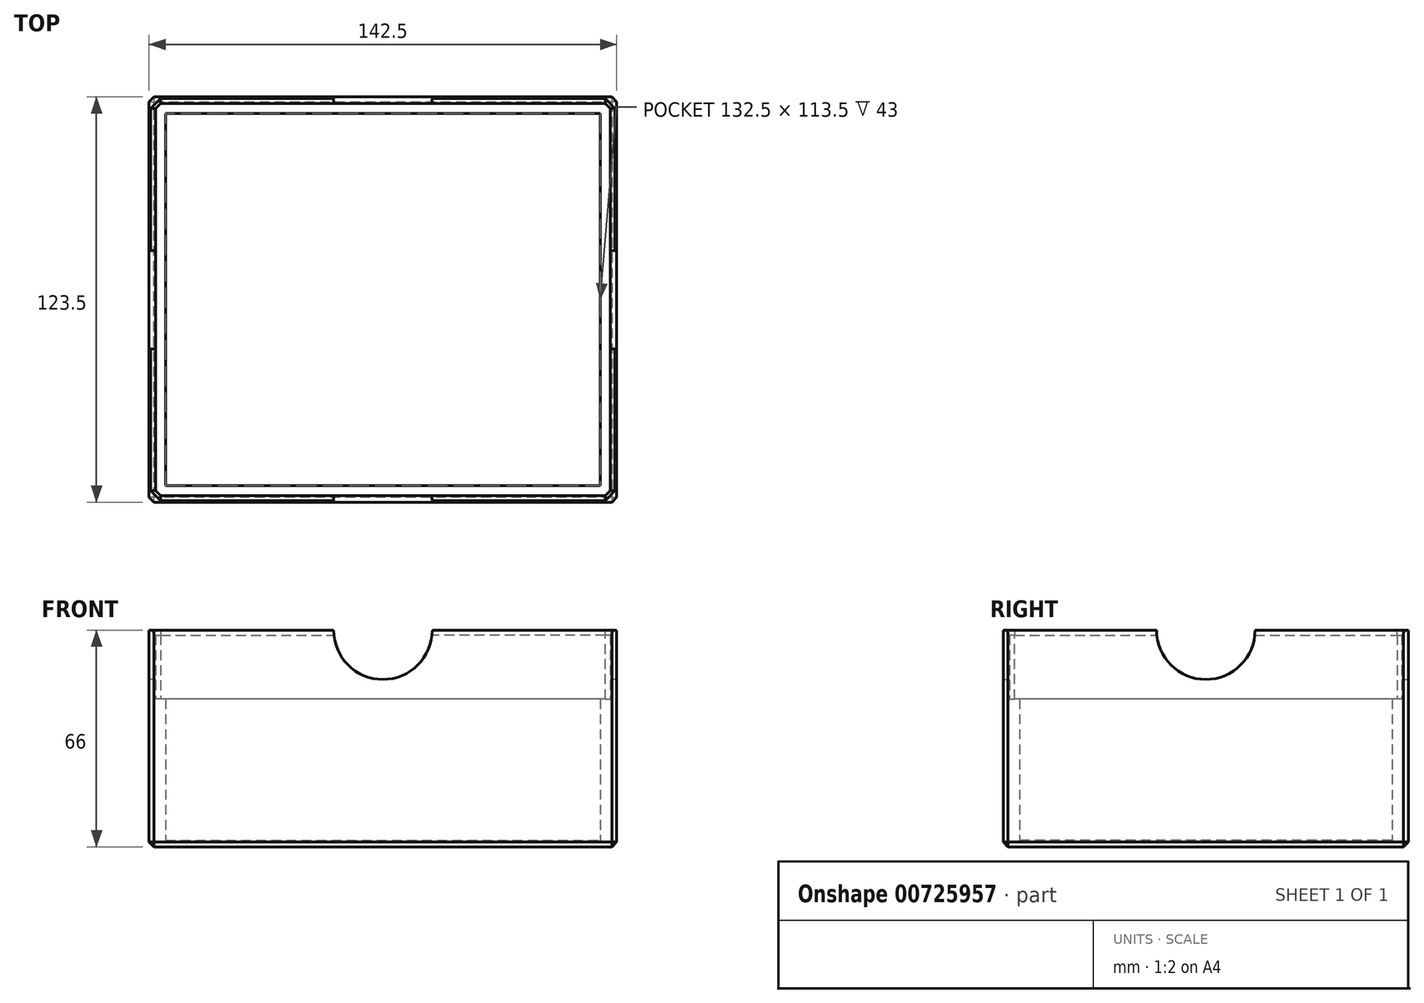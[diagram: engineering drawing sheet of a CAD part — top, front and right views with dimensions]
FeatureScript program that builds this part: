
annotation { "Feature Type Name" : "Feature", "Feature Type Description" : "" }
export const myFeature = defineFeature(function(context is Context, id is Id, definition is map)
    precondition{}
    {
        {
            var Q0;
            Q0=qCreatedBy(makeId("Top.planeOp"),FACE);
            var sketch = newSketch(context, id + "F0", { "sketchPlane" : qUnion([Q0])});
            skLineSegment(sketch, "E0.bottom", {"start": v(-69.25, 59.75) * mm, "end": v(69.25, 59.75) * mm});
            skLineSegment(sketch, "E0.top", {"start": v(-69.25, -59.75) * mm, "end": v(69.25, -59.75) * mm});
            skLineSegment(sketch, "E0.left", {"start": v(-69.25, 59.75) * mm, "end": v(-69.25, -59.75) * mm});
            skLineSegment(sketch, "E0.right", {"start": v(69.25, 59.75) * mm, "end": v(69.25, -59.75) * mm});
            skPoint(sketch, "E0.middle", {"position": v(0, 0) * mm});
            skLineSegment(sketch, "E1.0", {"start": v(-71.25, 61.75) * mm, "end": v(71.25, 61.75) * mm});
            skLineSegment(sketch, "E1.1", {"start": v(-71.25, 61.75) * mm, "end": v(-71.25, -61.75) * mm});
            skLineSegment(sketch, "E1.2", {"start": v(-71.25, -61.75) * mm, "end": v(71.25, -61.75) * mm});
            skLineSegment(sketch, "E1.3", {"start": v(71.25, 61.75) * mm, "end": v(71.25, -61.75) * mm});
            skSolve(sketch);
        }
        {
            var Q0;
            Q0=makeQuery(id+"F0.imprint","IMPRINT",FACE,{"disambiguationData":[TD([[makeQuery(id+"F0.imprint","IMPRINT",EDGE,{"derivedFrom":sQuery(id+"F0.wireOp",EDGE,"E0.bottom")}),1.0]])]});
            extrude(context, id + "F1", {"entities" : qUnion([Q0]), "depth" : 66 * mm, "offsetDistance" : 25 * mm});
        }
        {
            var Q0;
            Q0=makeQuery(id+"F0.imprint","IMPRINT",FACE,{"disambiguationData":[TD([[makeQuery(id+"F0.imprint","IMPRINT",EDGE,{"derivedFrom":sQuery(id+"F0.wireOp",EDGE,"E0.bottom")}),-1.0]])]});
            extrude(context, id + "F2", {"entities" : qUnion([Q0]), "operationType" : NewBodyOperationType.ADD, "depth" : 2 * mm, "offsetDistance" : 25 * mm});
        }
        {
            var Q0;
            Q0=makeQuery(id+"F1.opExtrude","SWEPT_FACE",FACE,{"disambiguationData":[OSD([sQuery(id+"F0.wireOp",EDGE,"E0.top")])]});
            var sketch = newSketch(context, id + "F3", { "sketchPlane" : qUnion([Q0])});
            skLineSegment(sketch, "E2.bottom", {"start": v(-69.25, 2) * mm, "end": v(69.25, 2) * mm});
            skLineSegment(sketch, "E2.top", {"start": v(-69.25, 45) * mm, "end": v(69.25, 45) * mm});
            skLineSegment(sketch, "E2.left", {"start": v(-69.25, 2) * mm, "end": v(-69.25, 45) * mm});
            skLineSegment(sketch, "E2.right", {"start": v(69.25, 2) * mm, "end": v(69.25, 45) * mm});
            skSolve(sketch);
        }
        {
            var Q0;
            Q0 = qSketchRegion(id + "F3", true);
            extrude(context, id + "F4", {"entities" : qUnion([Q0]), "operationType" : NewBodyOperationType.ADD, "depth" : 3 * mm, "offsetDistance" : 25 * mm});
        }
        {
            var Q0;
            Q0=makeQuery(id+"F1.opExtrude","SWEPT_FACE",FACE,{"disambiguationData":[OSD([sQuery(id+"F0.wireOp",EDGE,"E0.left")])]});
            var sketch = newSketch(context, id + "F5", { "sketchPlane" : qUnion([Q0])});
            skLineSegment(sketch, "E3.bottom", {"start": v(-56.75, 45) * mm, "end": v(59.75, 45) * mm});
            skLineSegment(sketch, "E3.top", {"start": v(-56.75, 2) * mm, "end": v(59.75, 2) * mm});
            skLineSegment(sketch, "E3.left", {"start": v(-56.75, 45) * mm, "end": v(-56.75, 2) * mm});
            skLineSegment(sketch, "E3.right", {"start": v(59.75, 45) * mm, "end": v(59.75, 2) * mm});
            skSolve(sketch);
        }
        {
            var Q0;
            Q0 = qSketchRegion(id + "F5", true);
            extrude(context, id + "F6", {"entities" : qUnion([Q0]), "operationType" : NewBodyOperationType.ADD, "depth" : 3 * mm, "offsetDistance" : 25 * mm});
        }
        {
            var Q0;
            Q0=makeQuery(id+"F1.opExtrude","SWEPT_FACE",FACE,{"disambiguationData":[OSD([sQuery(id+"F0.wireOp",EDGE,"E0.bottom")])]});
            var sketch = newSketch(context, id + "F7", { "sketchPlane" : qUnion([Q0])});
            skLineSegment(sketch, "E4.bottom", {"start": v(-66.25, 45) * mm, "end": v(69.25, 45) * mm});
            skLineSegment(sketch, "E4.top", {"start": v(-66.25, 2) * mm, "end": v(69.25, 2) * mm});
            skLineSegment(sketch, "E4.left", {"start": v(-66.25, 45) * mm, "end": v(-66.25, 2) * mm});
            skLineSegment(sketch, "E4.right", {"start": v(69.25, 45) * mm, "end": v(69.25, 2) * mm});
            skSolve(sketch);
        }
        {
            var Q0;
            Q0 = qSketchRegion(id + "F7", true);
            extrude(context, id + "F8", {"entities" : qUnion([Q0]), "operationType" : NewBodyOperationType.ADD, "depth" : 3 * mm, "offsetDistance" : 25 * mm});
        }
        {
            var Q0;
            Q0=makeQuery(id+"F1.opExtrude","SWEPT_FACE",FACE,{"disambiguationData":[OSD([sQuery(id+"F0.wireOp",EDGE,"E0.right")])]});
            var sketch = newSketch(context, id + "F9", { "sketchPlane" : qUnion([Q0])});
            skLineSegment(sketch, "E5.bottom", {"start": v(-56.75, 45) * mm, "end": v(56.75, 45) * mm});
            skLineSegment(sketch, "E5.top", {"start": v(-56.75, 2) * mm, "end": v(56.75, 2) * mm});
            skLineSegment(sketch, "E5.left", {"start": v(-56.75, 45) * mm, "end": v(-56.75, 2) * mm});
            skLineSegment(sketch, "E5.right", {"start": v(56.75, 45) * mm, "end": v(56.75, 2) * mm});
            skSolve(sketch);
        }
        {
            var Q0;
            Q0 = qSketchRegion(id + "F9", true);
            extrude(context, id + "F10", {"entities" : qUnion([Q0]), "operationType" : NewBodyOperationType.ADD, "depth" : 3 * mm, "offsetDistance" : 25 * mm});
        }
        {
            var Q0;
            Q0=makeQuery(id+"F1.opExtrude","SWEPT_EDGE",EDGE,{"disambiguationData":[OSD([sQuery(id+"F0.wireOp",EDGE,"E1.0"),sQuery(id+"F0.wireOp",EDGE,"E1.1")])]});
            var Q1;
            Q1=makeQuery(id+"F1.opExtrude","SWEPT_EDGE",EDGE,{"disambiguationData":[OSD([sQuery(id+"F0.wireOp",EDGE,"E1.1"),sQuery(id+"F0.wireOp",EDGE,"E1.2")])]});
            var Q2;
            Q2=makeQuery(id+"F1.opExtrude","SWEPT_EDGE",EDGE,{"disambiguationData":[OSD([sQuery(id+"F0.wireOp",EDGE,"E1.2"),sQuery(id+"F0.wireOp",EDGE,"E1.3")])]});
            var Q3;
            Q3=makeQuery(id+"F1.opExtrude","SWEPT_EDGE",EDGE,{"disambiguationData":[OSD([sQuery(id+"F0.wireOp",EDGE,"E1.0"),sQuery(id+"F0.wireOp",EDGE,"E1.3")])]});
            var Q4;
            Q4=makeQuery(id+"F1.opExtrude","CAP_EDGE",EDGE,{"disambiguationData":[OSD([sQuery(id+"F0.wireOp",EDGE,"E1.3")])],"isStart":true});
            var Q5;
            Q5=makeQuery(id+"F1.opExtrude","CAP_EDGE",EDGE,{"disambiguationData":[OSD([sQuery(id+"F0.wireOp",EDGE,"E1.0")])],"isStart":true});
            var Q6;
            Q6=makeQuery(id+"F1.opExtrude","CAP_EDGE",EDGE,{"disambiguationData":[OSD([sQuery(id+"F0.wireOp",EDGE,"E1.1")])],"isStart":true});
            var Q7;
            Q7=makeQuery(id+"F1.opExtrude","CAP_EDGE",EDGE,{"disambiguationData":[OSD([sQuery(id+"F0.wireOp",EDGE,"E1.2")])],"isStart":true});
            var Q8;
            Q8=makeQuery(id+"F1.opExtrude","CAP_EDGE",EDGE,{"disambiguationData":[OSD([sQuery(id+"F0.wireOp",EDGE,"E0.right")])],"isStart":false});
            var Q9;
            Q9=makeQuery(id+"F1.opExtrude","CAP_EDGE",EDGE,{"disambiguationData":[OSD([sQuery(id+"F0.wireOp",EDGE,"E0.top")])],"isStart":false});
            var Q10;
            Q10=makeQuery(id+"F1.opExtrude","CAP_EDGE",EDGE,{"disambiguationData":[OSD([sQuery(id+"F0.wireOp",EDGE,"E0.bottom")])],"isStart":false});
            var Q11;
            Q11=makeQuery(id+"F1.opExtrude","CAP_EDGE",EDGE,{"disambiguationData":[OSD([sQuery(id+"F0.wireOp",EDGE,"E0.left")])],"isStart":false});
            var Q12;
            Q12=makeQuery(id+"F1.opExtrude","SWEPT_EDGE",EDGE,{"disambiguationData":[OSD([sQuery(id+"F0.wireOp",EDGE,"E0.bottom"),sQuery(id+"F0.wireOp",EDGE,"E0.right")])]});
            var Q13;
            Q13=makeQuery(id+"F10.opExtrude","CAP_EDGE",EDGE,{"disambiguationData":[OSD([sQuery(id+"F9.wireOp",EDGE,"E5.left")])],"isStart":false});
            var Q14;
            Q14=makeQuery(id+"F10.opExtrude","CAP_EDGE",EDGE,{"disambiguationData":[OSD([sQuery(id+"F9.wireOp",EDGE,"E5.right")])],"isStart":false});
            var Q15;
            Q15=makeQuery(id+"F1.opExtrude","SWEPT_EDGE",EDGE,{"disambiguationData":[OSD([sQuery(id+"F0.wireOp",EDGE,"E0.top"),sQuery(id+"F0.wireOp",EDGE,"E0.right")])]});
            var Q16;
            Q16=makeQuery(id+"F1.opExtrude","SWEPT_EDGE",EDGE,{"disambiguationData":[OSD([sQuery(id+"F0.wireOp",EDGE,"E0.bottom"),sQuery(id+"F0.wireOp",EDGE,"E0.left")])]});
            var Q17;
            Q17=makeQuery(id+"F8.opExtrude","CAP_EDGE",EDGE,{"disambiguationData":[OSD([sQuery(id+"F7.wireOp",EDGE,"E4.left")])],"isStart":false});
            var Q18;
            Q18=makeQuery(id+"F1.opExtrude","SWEPT_EDGE",EDGE,{"disambiguationData":[OSD([sQuery(id+"F0.wireOp",EDGE,"E0.top"),sQuery(id+"F0.wireOp",EDGE,"E0.left")])]});
            var Q19;
            Q19=makeQuery(id+"F6.opExtrude","CAP_EDGE",EDGE,{"disambiguationData":[OSD([sQuery(id+"F5.wireOp",EDGE,"E3.left")])],"isStart":false});
            chamfer(context, id + "F11", {"entities" : qUnion([Q0, Q1, Q2, Q3, Q4, Q5, Q6, Q7, Q8, Q9, Q10, Q11, Q12, Q13, Q14, Q15, Q16, Q17, Q18, Q19]), "width" : 1.5 * mm, "tangentPropagation" : true});
        }
        {
            var Q0;
            Q0=makeQuery(id+"F1.opExtrude","SWEPT_FACE",FACE,{"disambiguationData":[OSD([sQuery(id+"F0.wireOp",EDGE,"E1.0")])]});
            var sketch = newSketch(context, id + "F12", { "sketchPlane" : qUnion([Q0])});
            skCircle(sketch, "E6", {"center": v(0, 66) * mm, "radius": 15 * mm});
            skSolve(sketch);
        }
        {
            var Q0;
            Q0 = qSketchRegion(id + "F12", true);
            var Q1;
            Q1=makeQuery(id+"F1.opExtrude","SWEPT_FACE",FACE,{"disambiguationData":[OSD([sQuery(id+"F0.wireOp",EDGE,"E1.2")])]});
            extrude(context, id + "F13", {"entities" : qUnion([Q0]), "operationType" : NewBodyOperationType.REMOVE, "endBound" : BoundingType.UP_TO_SURFACE, "oppositeDirection" : true, "depth" : 25 * mm, "endBoundEntityFace" : qUnion([Q1]), "offsetDistance" : 25 * mm});
        }
        {
            var Q0;
            Q0=makeQuery(id+"F1.opExtrude","SWEPT_FACE",FACE,{"disambiguationData":[OSD([sQuery(id+"F0.wireOp",EDGE,"E1.1")])]});
            var sketch = newSketch(context, id + "F14", { "sketchPlane" : qUnion([Q0])});
            skCircle(sketch, "E7", {"center": v(0, 66) * mm, "radius": 15 * mm});
            skSolve(sketch);
        }
        {
            var Q0;
            Q0 = qSketchRegion(id + "F14", true);
            var Q1;
            Q1=makeQuery(id+"F1.opExtrude","SWEPT_FACE",FACE,{"disambiguationData":[OSD([sQuery(id+"F0.wireOp",EDGE,"E1.3")])]});
            extrude(context, id + "F15", {"entities" : qUnion([Q0]), "operationType" : NewBodyOperationType.REMOVE, "endBound" : BoundingType.UP_TO_SURFACE, "oppositeDirection" : true, "depth" : 25 * mm, "endBoundEntityFace" : qUnion([Q1]), "offsetDistance" : 25 * mm});
        }
    });
